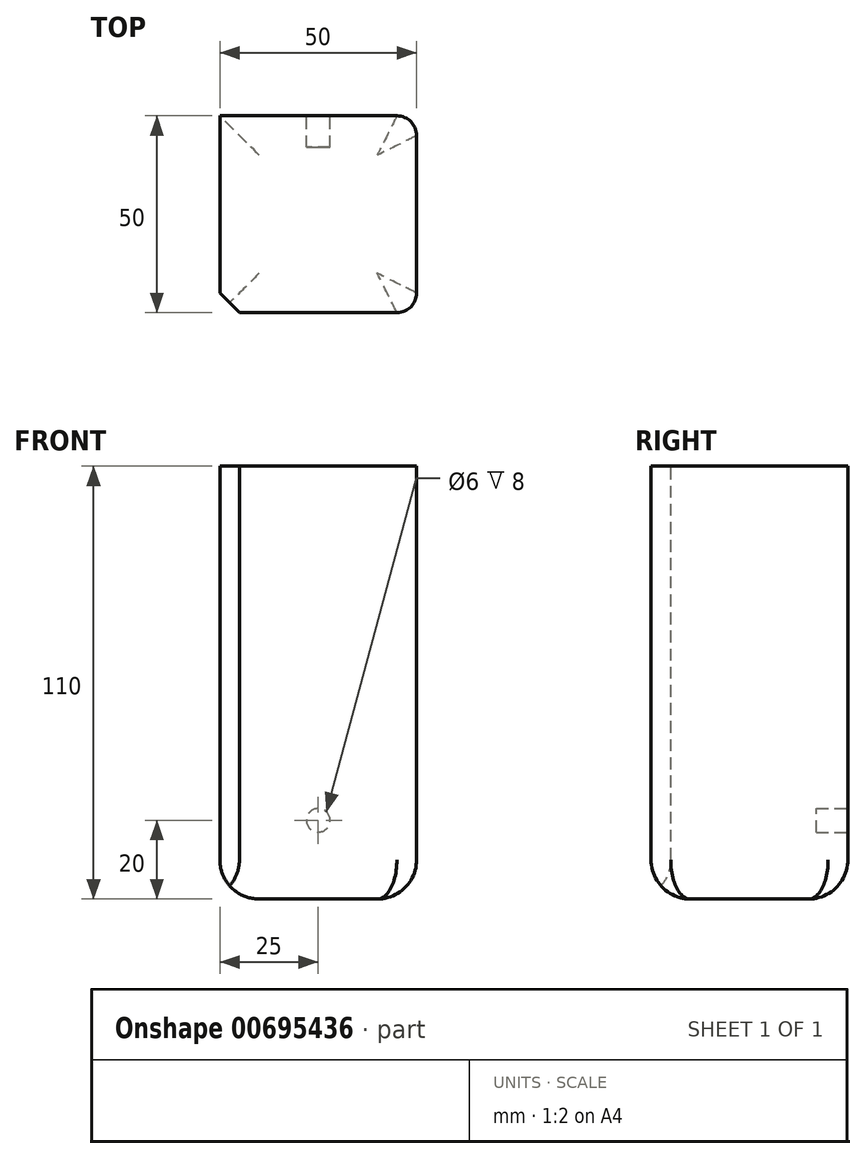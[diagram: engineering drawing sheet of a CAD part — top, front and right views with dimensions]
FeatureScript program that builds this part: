
annotation { "Feature Type Name" : "Feature", "Feature Type Description" : "" }
export const myFeature = defineFeature(function(context is Context, id is Id, definition is map)
    precondition{}
    {
        {
            var Q0;
            Q0=qCreatedBy(makeId("Front.planeOp"),FACE);
            var sketch = newSketch(context, id + "F0", { "sketchPlane" : qUnion([Q0])});
            skLineSegment(sketch, "E0.bottom", {"start": v(-25, 90) * mm, "end": v(25, 90) * mm});
            skLineSegment(sketch, "E0.top", {"start": v(-25, -10) * mm, "end": v(25, -10) * mm});
            skLineSegment(sketch, "E0.left", {"start": v(-25, 90) * mm, "end": v(-25, -10) * mm});
            skLineSegment(sketch, "E0.right", {"start": v(25, 90) * mm, "end": v(25, -10) * mm});
            skSolve(sketch);
        }
        {
            var Q0;
            Q0=makeQuery(id+"F0.imprint","IMPRINT",FACE,{"disambiguationData":[TD([[makeQuery(id+"F0.imprint","IMPRINT",EDGE,{"derivedFrom":sQuery(id+"F0.wireOp",EDGE,"E0.bottom")}),-1.0]])]});
            extrude(context, id + "F1", {"entities" : qUnion([Q0]), "depth" : 50 * mm, "offsetDistance" : 25 * mm});
        }
        {
            var Q0;
            Q0=qCreatedBy(makeId("Front.planeOp"),FACE);
            var sketch = newSketch(context, id + "F2", { "sketchPlane" : qUnion([Q0])});
            skCircle(sketch, "E1", {"center": v(0, 0) * mm, "radius": 3 * mm});
            skSolve(sketch);
        }
        {
            var Q0;
            Q0 = qSketchRegion(id + "F2", true);
            var Q1;
            Q1=sQuery(id+"F2.wireOp",EDGE,"E1");
            extrude(context, id + "F3", {"entities" : qUnion([Q0]), "operationType" : NewBodyOperationType.REMOVE, "surfaceEntities" : qUnion([Q1]), "depth" : 8 * mm, "offsetDistance" : 25 * mm});
        }
        {
            var Q0;
            Q0=makeQuery(id+"F1.opExtrude","CAP_EDGE",EDGE,{"disambiguationData":[OSD([sQuery(id+"F0.wireOp",EDGE,"E0.left")])],"isStart":false});
            chamfer(context, id + "F4", {"entities" : qUnion([Q0]), "width" : 5 * mm, "tangentPropagation" : true});
        }
        {
            var Q0;
            Q0=makeQuery(id+"F1.opExtrude","CAP_EDGE",EDGE,{"disambiguationData":[OSD([sQuery(id+"F0.wireOp",EDGE,"E0.right")])],"isStart":true});
            var Q1;
            Q1=makeQuery(id+"F1.opExtrude","CAP_EDGE",EDGE,{"disambiguationData":[OSD([sQuery(id+"F0.wireOp",EDGE,"E0.right")])],"isStart":false});
            fillet(context, id + "F5", {"entities" : qUnion([Q0, Q1]), "radius" : 5 * mm, "tangentPropagation" : true, "allowEdgeOverflow" : false});
        }
        {
            var Q0;
            Q0=makeQuery(id+"F1.opExtrude","SWEPT_FACE",FACE,{"disambiguationData":[OSD([sQuery(id+"F0.wireOp",EDGE,"E0.top")])]});
            extrude(context, id + "F6", {"entities" : qUnion([Q0]), "operationType" : NewBodyOperationType.ADD, "depth" : 10 * mm, "offsetDistance" : 25 * mm});
        }
        {
            var Q0;
            {var subQ0=sQuery(id+"F0.wireOp",EDGE,"E0.top");Q0=makeQuery(id+"F6.opExtrude","CAP_EDGE",EDGE,{"disambiguationData":[OSD([subQ0]),TDD([makeQuery(id+"F1.opExtrude","CAP_EDGE",EDGE,{"disambiguationData":[OSD([subQ0])],"isStart":true})])],"isStart":false});}
            var Q1;
            {var subQ0=sQuery(id+"F0.wireOp",EDGE,"E0.right");var subQ1=sQuery(id+"F0.wireOp",EDGE,"E0.top");Q1=makeQuery(id+"F6.opExtrude","CAP_EDGE",EDGE,{"disambiguationData":[OSD([subQ1,subQ0]),TDD([makeQuery(id+"F1.opExtrude","SWEPT_EDGE",EDGE,{"disambiguationData":[OSD([subQ1,subQ0])]})])],"isStart":false});}
            var Q2;
            {var subQ0=sQuery(id+"F0.wireOp",EDGE,"E0.top");Q2=makeQuery(id+"F6.opExtrude","CAP_EDGE",EDGE,{"disambiguationData":[OSD([subQ0]),TDD([makeQuery(id+"F1.opExtrude","CAP_EDGE",EDGE,{"disambiguationData":[OSD([subQ0])],"isStart":false})])],"isStart":false});}
            var Q3;
            {var subQ0=sQuery(id+"F0.wireOp",EDGE,"E0.left");var subQ1=sQuery(id+"F0.wireOp",EDGE,"E0.top");Q3=makeQuery(id+"F6.opExtrude","CAP_EDGE",EDGE,{"disambiguationData":[OSD([subQ1,subQ0]),TDD([makeQuery(id+"F1.opExtrude","SWEPT_EDGE",EDGE,{"disambiguationData":[OSD([subQ1,subQ0])]})])],"isStart":false});}
            fillet(context, id + "F7", {"entities" : qUnion([Q0, Q1, Q2, Q3]), "radius" : 10 * mm, "tangentPropagation" : true, "allowEdgeOverflow" : false});
        }
    });
